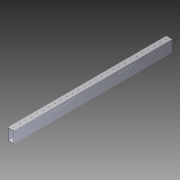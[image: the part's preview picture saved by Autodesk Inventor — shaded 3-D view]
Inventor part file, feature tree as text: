
AUTODESK INVENTOR PART (.ipt)
format: ipt  version: 2014 SP1 (Build 180222100, 222)  size: 855,040 bytes
history: native  units: in
note: dims shown in document units (in); Inventor stores cm internally (conversion verified against a paired STEP export)
features: reference x11, extrude x3, sketch x3, other x2, imported_body x1
ambient origin geometry x8: Origin, YZ Plane, XZ Plane, XY Plane, X Axis, Y Axis, Z Axis, Center Point
bodies: Body1 (feature_tree)
feature tree (20):
  other  "Cut-Extrude2"
  other  "217-3453-STEP1"
  extrude  "Extrusion1"  Depth=15.9375in TaperAngle=0.0deg
  extrude  "Extrusion2"  [1 undecoded]
  extrude  "Extrusion3"  [1 undecoded]
  imported_body  "Base1"
  sketch  "Sketch1"  dims[d0=15.9375in d1=0.0in d2=15.9375in d3=0.0in]
  sketch  "Sketch2"  dims[d4=1.0in d5=0.0in]
  sketch  "Sketch3"
  reference  "Reference1"
  reference  "Reference2"
  reference  "Reference3"
  reference  "Reference4"
  reference  "Reference5"
  reference  "Reference6"
  reference  "Reference7"
  reference  "Reference8"
  reference  "Reference9"
  reference  "Reference10"
  reference  "Reference11"
note: 2 required parameter values undecoded (feature->parameter linkage not recoverable at this tier; creation-order binding heuristic only, values carry confidence <= 0.55)
